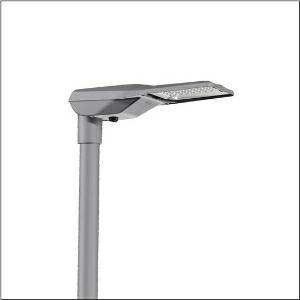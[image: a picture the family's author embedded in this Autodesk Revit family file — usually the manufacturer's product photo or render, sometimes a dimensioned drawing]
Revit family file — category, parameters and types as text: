
# Revit family: streetlight_sl_21_mini___p0_5a_5xe2v33r08hb_69df
name_source: partatom
category: Lighting Fixtures
units: mm (PartAtom-declared; Revit-internal decimal feet)

## family parameters
Cut with Voids When Loaded = No
Host = Face
Light Source = No
Part Type = Normal
Room Calculation Point = No
Round Connector Dimension = Use Diameter
Shared = No

## types (1)
- --- (1 x LED, 8890 lm, 66 W, 3000K)
    Apparent Load = 66 VA
    CIE Flux Codes = 37 73 96 100 100
    Color Rendering = 70
    Color Temperature = 3000K
    Default Elevation = 1800 mm
    Description = Streetlight SL 21 mini, mast luminaire, primary light control with lens, of PMMA, primary optical cover: cover, of toughened safety glass, transparent, light distribution: P0.5a, light emission: direct distribution, primary light characteristic: asymmetric, installation type: post-top, side-entry, LED, High Power LED, rated luminous flux: 8.890lm, luminous efficacy: 135lm/W, light colour: 730, colour temperature: 3000K, control gear: D4i, control: pre-setting: logarithmic dimming characteristic, flexible luminous flux parameterisation, time-dependent luminous flux control, constant luminous flux control, overheat protection, mains connection: 220..240V, AC, 50/60Hz, start of lifetime: 66W, end of service life: 69W, reduction: 30W, luminaire housing, of diecast aluminium, powder-coated, Siteco® metallic grey (DB 702S), corrosivity category C5 mid according to DIN EN ISO 12944, multi-level sealing system, sealing non-destructively replaceable, inclination adjustable: 0°, 5°, 10°, 15°, please order mast flange separately, length: 628mm, width: 235mm, height: 110mm, mast flange for spigot size: 42mm (side-entry): 5XC10008XM4, 60/48mm (side-entry/post-top): 5XC10108XM2, 76/60mm (side-entry/post-top): 5XC10108XM1, mounting height: 4..8m, Smart Interface below, protection rating (complete): IP66, insulation class (complete): insulation class II (safety insulation), certification: CE, ENEC, ENEC+, VDE, impact resistance: IK10, permissible operating ambient temperature for outdoor applications: -40..+50°C, standard-compliant lighting for roads and squares, packaging unit: 1 piece

Light Distribution: P0.5a
    Height = 110 mm
    Lamp = 1 x LED
    Lamp Light Flux = 8890 lm
    Lamp Power = 66 W
    Lamp count = 1
    Length = 625 mm
    Luminous efficacy = 135 lm/W
    Manufacturer = Siteco
    ModVariant = No
    Model = 5XE2V33R08HB
    Number of Poles = 1
    OnlyDefault = Yes
    Power Factor = 1
    Product Name = Streetlight SL 21 mini | P0.5a
    Product group = mast luminaire | pylon top
    ProductGroupID = 6100
    Protection Class = Protection class II
    Protection Degree = IP 66
    RLX_Detail_Level = 1
    RLX_Emergency_Light_Flux = 0 lm
    RLX_Emergency_Type = 0
    RLX_Emergency_Type_DB = No
    RlxData = <blob elided: 91765 chars, md5=789aa9df>
    Socket = socket
    Standby Power = 0 W
    System Light Flux = 8890 lm
    System Power = 66 W
    Type Comments = factory setting: luminous flux: 100 % | dim-lin: 254 | 670 mA
    Type Image = l_1003516.jpg
    URL = http://relux.com
    VarID = @adj_091363
    Voltage = 0 V
    Weight = 0.00 kg
    Width = 234 mm

## geometry (parser evidence)
native form markers: Blend x4, Sweep x12
no freeform markers — native parametric forms only
